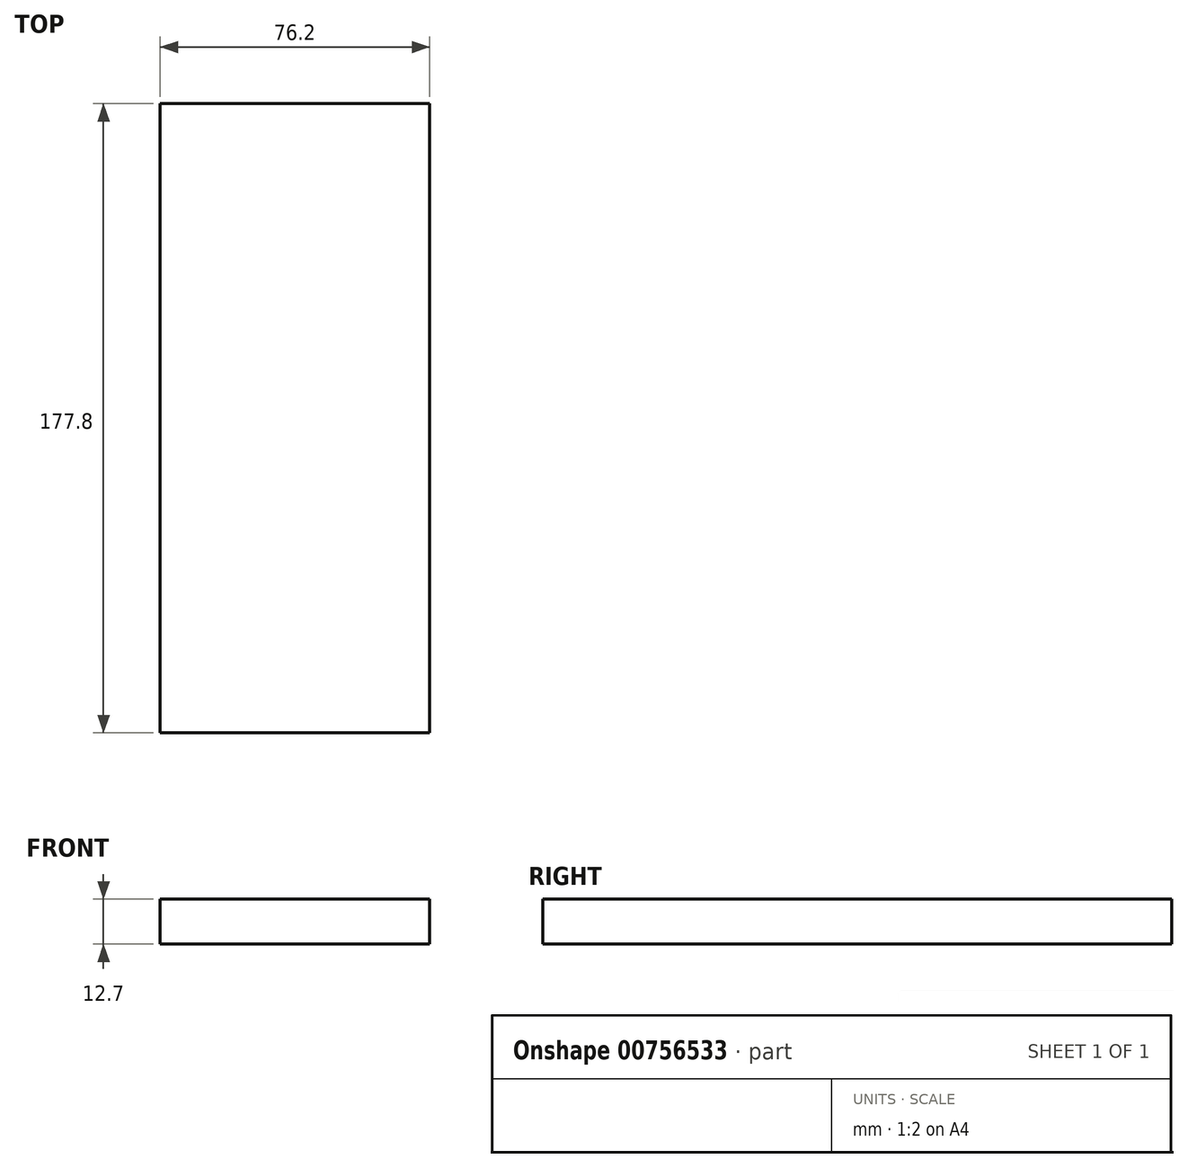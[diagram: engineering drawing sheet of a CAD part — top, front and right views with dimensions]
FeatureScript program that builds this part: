
annotation { "Feature Type Name" : "Feature", "Feature Type Description" : "" }
export const myFeature = defineFeature(function(context is Context, id is Id, definition is map)
    precondition{}
    {
        {
            var Q0;
            Q0=qCreatedBy(makeId("Top.planeOp"),FACE);
            var sketch = newSketch(context, id + "F0", { "sketchPlane" : qUnion([Q0])});
            skLineSegment(sketch, "E0.bottom", {"start": v(-60.46, 67.7) * mm, "end": v(15.74, 67.7) * mm});
            skLineSegment(sketch, "E0.top", {"start": v(-60.46, -110.1) * mm, "end": v(15.74, -110.1) * mm});
            skLineSegment(sketch, "E0.left", {"start": v(-60.46, 67.7) * mm, "end": v(-60.46, -110.1) * mm});
            skLineSegment(sketch, "E0.right", {"start": v(15.74, 67.7) * mm, "end": v(15.74, -110.1) * mm});
            skSolve(sketch);
        }
        {
            var Q0;
            Q0 = qSketchRegion(id + "F0", true);
            extrude(context, id + "F1", {"entities" : qUnion([Q0]), "depth" : 12.7 * mm, "offsetDistance" : 25.4 * mm});
        }
    });
